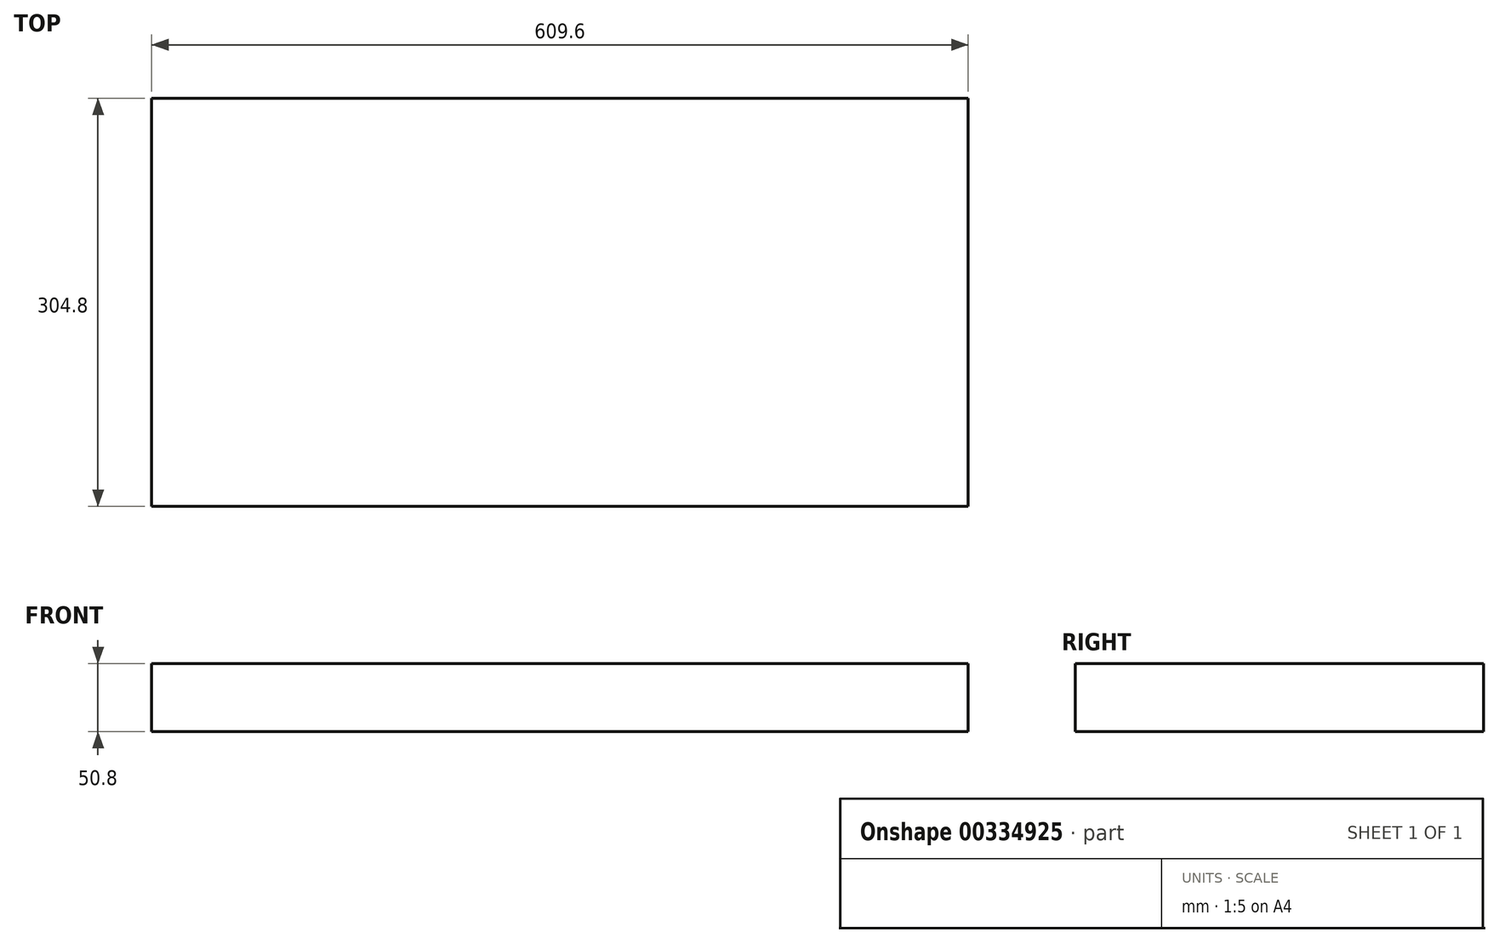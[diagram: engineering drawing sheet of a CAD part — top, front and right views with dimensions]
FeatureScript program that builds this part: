
annotation { "Feature Type Name" : "Feature", "Feature Type Description" : "" }
export const myFeature = defineFeature(function(context is Context, id is Id, definition is map)
    precondition{}
    {
        {
            var Q0;
            Q0=qCreatedBy(makeId("Top.planeOp"),FACE);
            var sketch = newSketch(context, id + "F0", { "sketchPlane" : qUnion([Q0])});
            skLineSegment(sketch, "E0.bottom", {"start": v(-46.38, 281.22) * mm, "end": v(563.22, 281.22) * mm});
            skLineSegment(sketch, "E0.top", {"start": v(-46.38, -23.58) * mm, "end": v(563.22, -23.58) * mm});
            skLineSegment(sketch, "E0.left", {"start": v(-46.38, 281.22) * mm, "end": v(-46.38, -23.58) * mm});
            skLineSegment(sketch, "E0.right", {"start": v(563.22, 281.22) * mm, "end": v(563.22, -23.58) * mm});
            skSolve(sketch);
        }
        {
            var Q0;
            Q0 = qSketchRegion(id + "F0", true);
            extrude(context, id + "F1", {"entities" : qUnion([Q0]), "depth" : 50.8 * mm});
        }
    });
